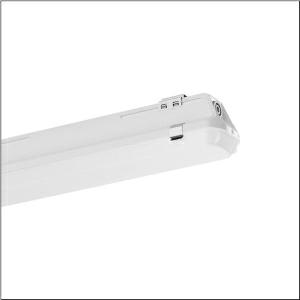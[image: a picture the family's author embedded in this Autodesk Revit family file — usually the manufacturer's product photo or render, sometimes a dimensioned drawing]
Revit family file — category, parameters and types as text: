
# Revit family: monsun_r__21_51fb10dp360b_a0ac
name_source: partatom
category: Lighting Fixtures
units: mm (PartAtom-declared; Revit-internal decimal feet)

## family parameters
Cut with Voids When Loaded = No
Host = Face
Light Source = No
Part Type = Normal
Room Calculation Point = No
Round Connector Dimension = Use Diameter
Shared = No

## types (1)
- --- (1 x LED, 6060 lm, 43.2 W, 3000K)
    Apparent Load = 43 VA
    CIE Flux Codes = 47 77 93 94 100
    Color Rendering = 80
    Color Temperature = 3000K
    Default Elevation = 1800 mm
    Description = Monsun® 21, damp-proof luminaire, chain hanger, primary optical cover: enclosure, of PMMA, light emission: direct distribution, primary light characteristic: symmetric, installation type: suspended mounting, surface-mounted, horizontal mounting, vertical mounting, LED, rated luminous flux: 6.060lm, luminous efficacy: 154lm/W, light colour: 830, colour temperature: 3000K, control gear: ECG DALI, with terminal, 5-pole, max. 2.5mm², mains connection: 220..240V, AC, 50/60Hz, rated input power: 39W, housing, of glass-fibre reinforced polyester, uncoated, bright grey, incl. chain hanger, length: 1.590mm, width: 90mm, height: 88mm, clip for enclosure, of stainless steel (V2A), ceiling mounting element, of stainless steel (V2A), chain hanger, of stainless steel (V2A), protection rating (complete): IP66, insulation class (complete): insulation class I (protective earthing), certification: CE, ENEC, VDE, UKCA, protection symbol: D, impact resistance: IK04, permissible operating ambient temperature: -25..+35°C, standard: EN 50419, EN 60598-2-1, corresponds to IFS (International Featured Standards) requirements for safety and quality in the food industry, for indoor or canopied outdoor use, no direct snow, no direct sun, no direct rain, contact your sales advisor before using the luminaires in applications with unclear chemical exposure, large temperature fluctuations or condensation-forming humidity, LABS conformity tested according to VDMA 24364:2018-05, packaging unit: 1 piece
    Height = 89 mm
    Lamp = 1 x LED
    Lamp Light Flux = 6060 lm
    Lamp Power = 43.2 W
    Lamp count = 1
    Length = 1590 mm
    Luminous efficacy = 140 lm/W
    Manufacturer = Siteco
    ModVariant = No
    Model = 51FB10DP360B
    Mounting Place = Ceiling
    Mounting Type = Surface mounted
    Number of Poles = 1
    OnlyDefault = Yes
    Power Factor = 1
    Product Name = Monsun® 21
    Product group = damp-proof luminaire
    ProductGroupID = 300
    Protection Class = Protection class I
    Protection Degree = IP 66
    RLX_Detail_Level = 1
    RLX_Emergency_Light_Flux = 0 lm
    RLX_Emergency_Type = 0
    RLX_Emergency_Type_DB = No
    RlxData = <blob elided: 92853 chars, md5=ad778a27>
    Socket = socket
    Standby Power = 0 W
    System Light Flux = 6060 lm
    System Power = 43 W
    Type Comments = factory setting: luminous flux: 100 % | dim-lin: 254 | 286 mA
    Type Image = l_1006717.jpg
    URL = http://relux.com
    VarID = @adj_078863
    Voltage = 0 V
    Weight = 0.00 kg
    Width = 90 mm

## geometry (parser evidence)
native form markers: Blend x4, Sweep x12
no freeform markers — native parametric forms only
